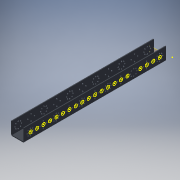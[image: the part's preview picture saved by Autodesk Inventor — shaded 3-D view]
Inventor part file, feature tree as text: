
AUTODESK INVENTOR PART (.ipt)
format: ipt  version: 2016 (Build 200138000, 138)  size: 610,304 bytes
history: native  units: in
note: dims shown in document units (in); Inventor stores cm internally (conversion verified against a paired STEP export)
features: other x214, reference x132, sketch x5, hole x4, plane x1, extrude x1
ambient origin geometry x8: Origin, YZ Plane, XZ Plane, XY Plane, X Axis, Y Axis, Z Axis, Center Point
bodies: Body1 (feature_tree)
feature tree (357):
  other  "A_1"
  other  "A_78"
  other  "A_79"
  other  "A_80"
  other  "A_81"
  other  "A_82"
  other  "A_83"
  other  "A_84"
  other  "A_85"
  other  "A_27"
  other  "A_86"
  other  "A_87"
  other  "A_88"
  other  "A_89"
  other  "A_90"
  other  "A_91"
  other  "A_92"
  other  "A_93"
  other  "A_119"
  other  "A_120"
  other  "A_121"
  other  "A_122"
  other  "A_123"
  other  "A_124"
  other  "A_125"
  other  "A_126"
  other  "A_127"
  other  "A_149"
  other  "A_150"
  other  "A_151"
  other  "A_152"
  other  "A_153"
  other  "A_154"
  other  "A_155"
  other  "A_156"
  other  "A_157"
  other  "A_158"
  other  "A_159"
  other  "A_160"
  other  "A_161"
  other  "A_162"
  other  "A_163"
  other  "A_164"
  other  "A_165"
  other  "A_166"
  other  "Work Axis46"
  other  "Work Axis47"
  other  "Work Axis48"
  other  "Work Axis49"
  other  "Work Axis50"
  other  "Work Axis51"
  other  "Work Axis52"
  other  "Work Axis53"
  other  "Work Axis54"
  other  "Work Axis55"
  other  "Work Axis56"
  other  "Work Axis57"
  other  "Work Axis58"
  other  "Work Axis59"
  other  "Work Axis60"
  other  "Work Axis61"
  other  "Work Axis62"
  other  "Work Axis63"
  other  "A_18"
  other  "A_94"
  other  "A_95"
  other  "A_96"
  other  "A_97"
  other  "A_98"
  other  "A_99"
  other  "A_100"
  other  "A_101"
  other  "A_31"
  other  "A_102"
  other  "A_103"
  other  "A_104"
  other  "A_105"
  other  "A_106"
  other  "A_107"
  other  "A_108"
  other  "A_109"
  other  "A_128"
  other  "A_129"
  other  "A_130"
  other  "A_131"
  other  "A_132"
  other  "A_133"
  other  "A_134"
  other  "A_135"
  other  "A_136"
  other  "A_1283"
  other  "A_1284"
  other  "A_1285"
  other  "A_1286"
  other  "A_1287"
  other  "A_1288"
  other  "A_1289"
  other  "A_1290"
  other  "A_1291"
  other  "A_1292"
  other  "A_1293"
  other  "A_1294"
  other  "A_1295"
  other  "A_1296"
  other  "A_1297"
  other  "A_1298"
  other  "A_1299"
  other  "A_1300"
  other  "Work Axis109"
  other  "Work Axis110"
  other  "Work Axis111"
  other  "Work Axis112"
  other  "Work Axis113"
  other  "Work Axis114"
  other  "Work Axis115"
  other  "Work Axis116"
  other  "Work Axis117"
  other  "Work Axis118"
  other  "Work Axis119"
  other  "Work Axis120"
  other  "Work Axis121"
  other  "Work Axis122"
  other  "Work Axis123"
  other  "Work Axis124"
  other  "Work Axis125"
  other  "Work Axis126"
  other  "A_77"
  other  "A_110"
  other  "A_111"
  other  "A_112"
  other  "A_113"
  other  "A_139"
  other  "A_140"
  other  "A_141"
  other  "A_142"
  other  "A_143"
  other  "A_2421"
  other  "A_2422"
  other  "A_2423"
  other  "A_2424"
  other  "A_2425"
  other  "A_2426"
  other  "A_2427"
  other  "A_2428"
  other  "A_2429"
  other  "A_2430"
  other  "A_2449"
  other  "A_2450"
  other  "A_2451"
  other  "A_2452"
  other  "A_2453"
  other  "A_2454"
  other  "A_2455"
  other  "A_2456"
  other  "A_2457"
  other  "A_2458"
  other  "A_114"
  other  "A_115"
  other  "A_116"
  other  "A_117"
  other  "A_118"
  other  "A_144"
  other  "A_145"
  other  "A_146"
  other  "A_147"
  other  "A_148"
  other  "A_2431"
  other  "A_2432"
  other  "A_2433"
  other  "A_2434"
  other  "A_2435"
  other  "A_2436"
  other  "A_2437"
  other  "A_2438"
  other  "A_2439"
  other  "A_2440"
  other  "A_2459"
  other  "A_2460"
  other  "A_2461"
  other  "A_2462"
  other  "A_2463"
  other  "A_2464"
  other  "A_2465"
  other  "A_2466"
  other  "A_2467"
  other  "A_2468"
  other  "A_75"
  other  "A_76"
  other  "A_137"
  other  "A_138"
  other  "A_2441"
  other  "A_2442"
  other  "A_2443"
  other  "A_2444"
  other  "A_2469"
  other  "A_2470"
  other  "A_2471"
  other  "A_2472"
  other  "A_2417"
  other  "A_2418"
  other  "A_2419"
  other  "A_2420"
  other  "A_2445"
  other  "A_2446"
  other  "A_2447"
  other  "A_2448"
  other  "A_2473"
  other  "A_2474"
  other  "A_2475"
  other  "A_2476"
  other  "FRONT"
  other  "TOP"
  other  "RIGHT"
  other  "DTM1"
  plane  "Work Plane5"
  extrude  "Extrusion1"  [1 undecoded]
  hole  "Hole1"  [1 undecoded]
  hole  "Hole2"  [1 undecoded]
  hole  "Hole3"  [1 undecoded]
  hole  "Hole4"  [1 undecoded]
  sketch  "Sketch2"  dims[d0=13.8583in d1=0.0in]
  sketch  "Sketch3"  dims[d2=0.1457in d3=0.2362in d4=0.1575in d5=0.0787in d6=90.0deg d7=0.315in d8=0.8108in]
  reference  "Reference1"
  reference  "Reference2"
  reference  "Reference3"
  reference  "Reference4"
  reference  "Reference5"
  reference  "Reference6"
  reference  "Reference7"
  reference  "Reference8"
  reference  "Reference9"
  reference  "Reference10"
  reference  "Reference11"
  reference  "Reference12"
  reference  "Reference13"
  reference  "Reference14"
  reference  "Reference15"
  reference  "Reference16"
  reference  "Reference17"
  reference  "Reference18"
  reference  "Reference19"
  reference  "Reference20"
  reference  "Reference21"
  reference  "Reference22"
  reference  "Reference23"
  reference  "Reference24"
  reference  "Reference25"
  reference  "Reference26"
  reference  "Reference27"
  reference  "Reference28"
  reference  "Reference29"
  reference  "Reference30"
  reference  "Reference31"
  reference  "Reference32"
  reference  "Reference33"
  reference  "Reference34"
  reference  "Reference35"
  reference  "Reference36"
  reference  "Reference37"
  reference  "Reference38"
  reference  "Reference39"
  reference  "Reference40"
  reference  "Reference41"
  reference  "Reference42"
  reference  "Reference43"
  reference  "Reference44"
  reference  "Reference45"
  reference  "Reference46"
  reference  "Reference47"
  reference  "Reference48"
  reference  "Reference49"
  reference  "Reference50"
  reference  "Reference51"
  reference  "Reference52"
  reference  "Reference53"
  reference  "Reference54"
  reference  "Reference55"
  reference  "Reference56"
  reference  "Reference57"
  reference  "Reference58"
  reference  "Reference59"
  reference  "Reference60"
  reference  "Reference61"
  reference  "Reference62"
  reference  "Reference63"
  reference  "Reference64"
  reference  "Reference65"
  reference  "Reference66"
  reference  "Reference67"
  reference  "Reference68"
  reference  "Reference69"
  reference  "Reference70"
  reference  "Reference71"
  reference  "Reference72"
  reference  "Reference73"
  reference  "Reference74"
  reference  "Reference75"
  reference  "Reference76"
  reference  "Reference77"
  reference  "Reference78"
  reference  "Reference79"
  reference  "Reference80"
  reference  "Reference81"
  reference  "Reference82"
  reference  "Reference83"
  reference  "Reference84"
  reference  "Reference85"
  reference  "Reference86"
  reference  "Reference87"
  reference  "Reference88"
  reference  "Reference89"
  sketch  "Sketch4"  dims[d9=0.315in d10=0.2362in d11=0.1575in d12=0.0787in d13=90.0deg d14=0.315in d15=0.8108in]
  reference  "Reference90"
  reference  "Reference91"
  reference  "Reference92"
  reference  "Reference93"
  reference  "Reference94"
  reference  "Reference95"
  reference  "Reference96"
  reference  "Reference97"
  reference  "Reference98"
  reference  "Reference99"
  reference  "Reference100"
  reference  "Reference101"
  reference  "Reference102"
  reference  "Reference103"
  reference  "Reference104"
  reference  "Reference105"
  reference  "Reference106"
  reference  "Reference107"
  reference  "Reference108"
  reference  "Reference109"
  reference  "Reference110"
  sketch  "Sketch5"  dims[d16=0.1457in d17=0.2362in d18=0.1575in d19=0.0787in d20=90.0deg d21=0.315in d22=0.8108in]
  reference  "Reference111"
  sketch  "Sketch6"  dims[d23=0.315in d24=0.2362in d25=0.1575in d26=0.0787in d27=90.0deg d28=0.315in d29=0.8108in]
  reference  "Reference112"
  reference  "Reference113"
  reference  "Reference114"
  reference  "Reference115"
  reference  "Reference116"
  reference  "Reference117"
  reference  "Reference118"
  reference  "Reference119"
  reference  "Reference120"
  reference  "Reference121"
  reference  "Reference122"
  reference  "Reference123"
  reference  "Reference124"
  reference  "Reference125"
  reference  "Reference126"
  reference  "Reference127"
  reference  "Reference128"
  reference  "Reference129"
  reference  "Reference130"
  reference  "Reference131"
  reference  "Reference132"
note: 5 required parameter values undecoded (feature->parameter linkage not recoverable at this tier; creation-order binding heuristic only, values carry confidence <= 0.55)
